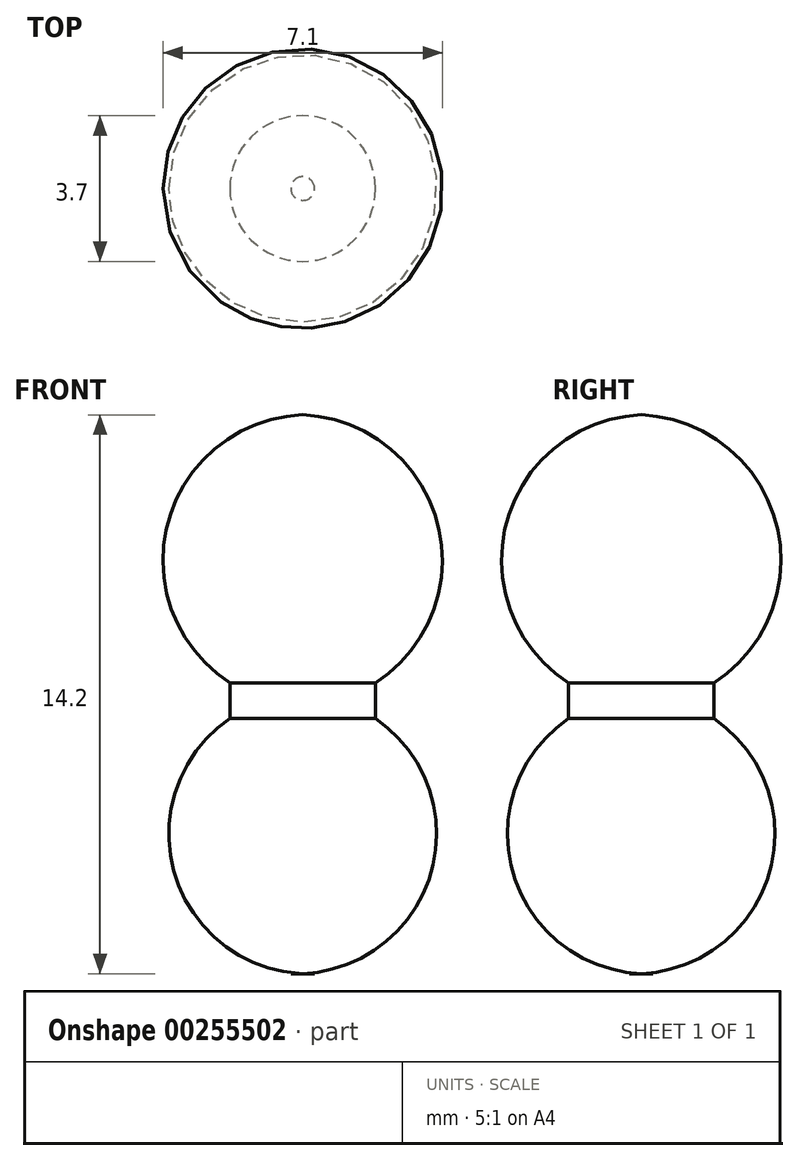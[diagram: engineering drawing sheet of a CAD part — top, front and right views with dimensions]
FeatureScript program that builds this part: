
annotation { "Feature Type Name" : "Feature", "Feature Type Description" : "" }
export const myFeature = defineFeature(function(context is Context, id is Id, definition is map)
    precondition{}
    {
        {
            var Q0;
            Q0=qCreatedBy(makeId("Front.planeOp"),FACE);
            var sketch = newSketch(context, id + "F0", { "sketchPlane" : qUnion([Q0])});
            skArc(sketch, "E0", {"start": v(-2, 2.93) * mm, "mid": v(-3.41, -0.97) * mm, "end": v(-0.15, -3.55) * mm});
            skLineSegment(sketch, "E1", {"start": v(-2, 3.84) * mm, "end": v(-2, 2.93) * mm});
            skArc(sketch, "E2.trimOffspring", {"start": v(-0.15, 10.65) * mm, "mid": v(-3.57, 7.93) * mm, "end": v(-2, 3.84) * mm});
            skPoint(sketch, "E3.center.orphan", {"position": v(0, 7.03) * mm});
            skLineSegment(sketch, "E4", {"start": v(-0.15, 10.65) * mm, "end": v(-0.15, -3.55) * mm});
            skPoint(sketch, "E5.MirrorCS.start.orphan", {"position": v(2, 3.84) * mm});
            skPoint(sketch, "E6.orphan", {"position": v(2, 2.93) * mm});
            skSolve(sketch);
        }
        {
            var Q0;
            Q0=makeQuery(id+"F0.imprint","IMPRINT",FACE,{"disambiguationData":[TD([[makeQuery(id+"F0.imprint","IMPRINT",EDGE,{"derivedFrom":sQuery(id+"F0.wireOp",EDGE,"E0")}),1.0]])]});
            var Q1;
            Q1=sQuery(id+"F0.wireOp",EDGE,"E4");
            revolve(context, id + "F1", {"entities" : qUnion([Q0]), "axis" : qUnion([Q1]), "revolveType" : RevolveType.FULL});
        }
    });
